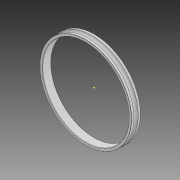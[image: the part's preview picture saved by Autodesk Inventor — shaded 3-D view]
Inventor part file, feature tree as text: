
AUTODESK INVENTOR PART (.ipt)
format: ipt  version: 2020 (Build 240168000, 168)  size: 139,264 bytes
history: native  units: in
note: dims shown in document units (in); Inventor stores cm internally (conversion verified against a paired STEP export)
features: sketch x1
ambient origin geometry x8: Origin, YZ Plane, XZ Plane, XY Plane, X Axis, Y Axis, Z Axis, Center Point
bodies: Solid2 (feature_tree), Solid1 (feature_tree)
feature tree (1):
  sketch  "Sketch1"
